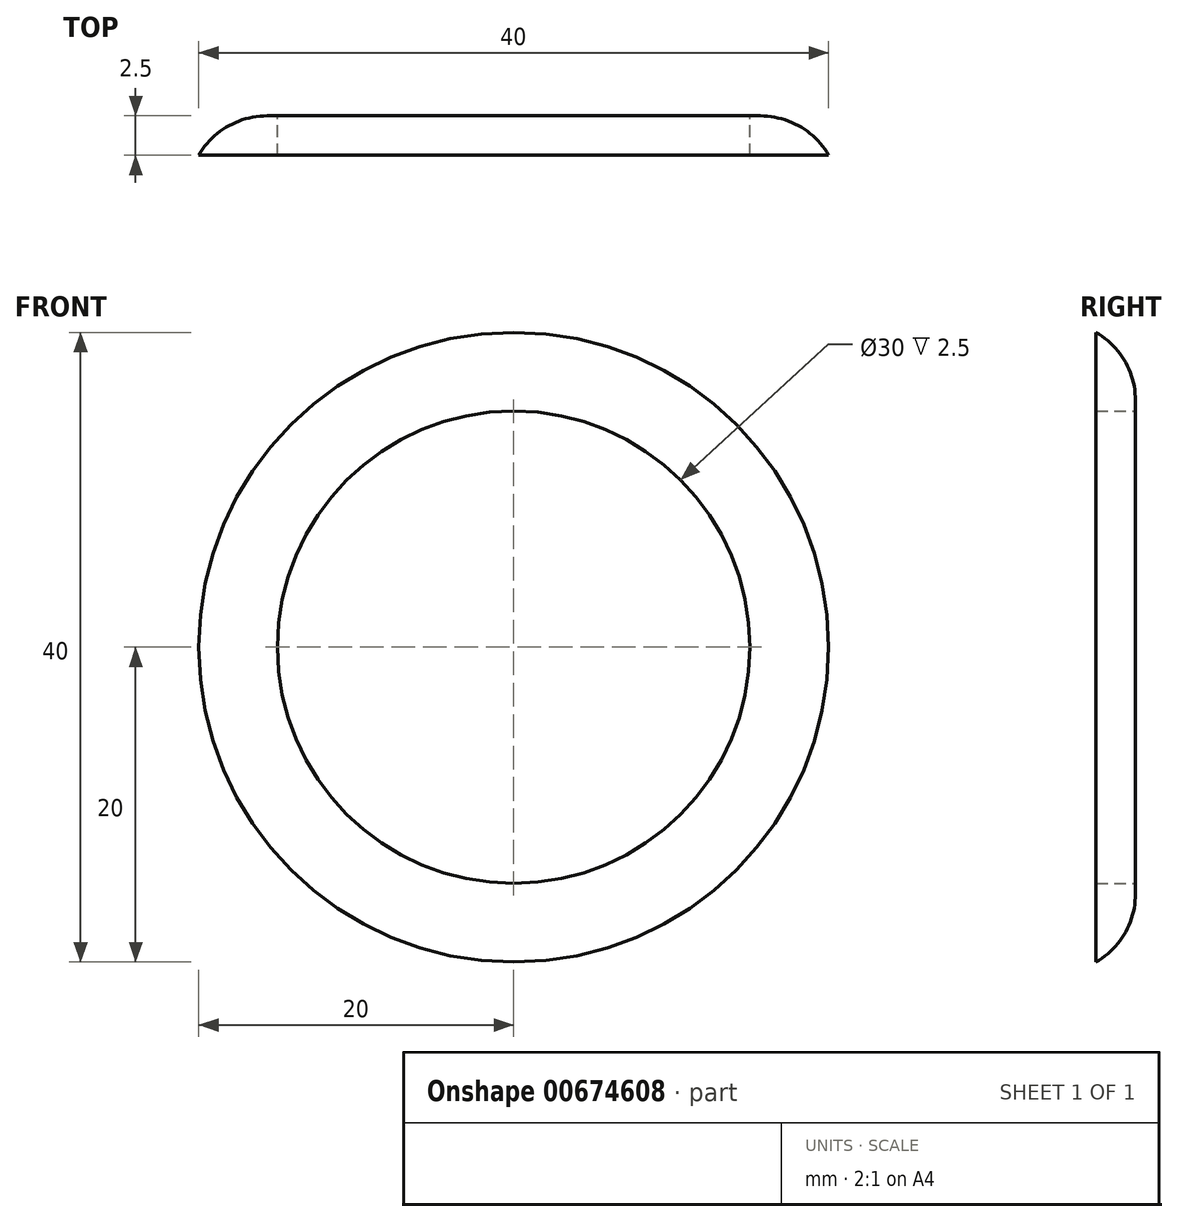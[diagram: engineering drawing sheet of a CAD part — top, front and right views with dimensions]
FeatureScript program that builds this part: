
annotation { "Feature Type Name" : "Feature", "Feature Type Description" : "" }
export const myFeature = defineFeature(function(context is Context, id is Id, definition is map)
    precondition{}
    {
        {
            var Q0;
            Q0=qCreatedBy(makeId("Front.planeOp"),FACE);
            var sketch = newSketch(context, id + "F0", { "sketchPlane" : qUnion([Q0])});
            skCircle(sketch, "E0", {"center": v(0, 0) * mm, "radius": 20 * mm});
            skCircle(sketch, "E1", {"center": v(0, 0) * mm, "radius": 15 * mm});
            skSolve(sketch);
        }
        {
            var Q0;
            Q0 = qSketchRegion(id + "F0", true);
            extrude(context, id + "F1", {"entities" : qUnion([Q0]), "depth" : 2.5 * mm, "offsetDistance" : 25 * mm});
        }
        {
            var Q0;
            Q0=makeQuery(id+"F1.opExtrude","CAP_EDGE",EDGE,{"disambiguationData":[OSD([sQuery(id+"F0.wireOp",EDGE,"E0")])],"isStart":true});
            fillet(context, id + "F2", {"entities" : qUnion([Q0]), "radius" : 5 * mm, "tangentPropagation" : true, "allowEdgeOverflow" : false});
        }
    });
